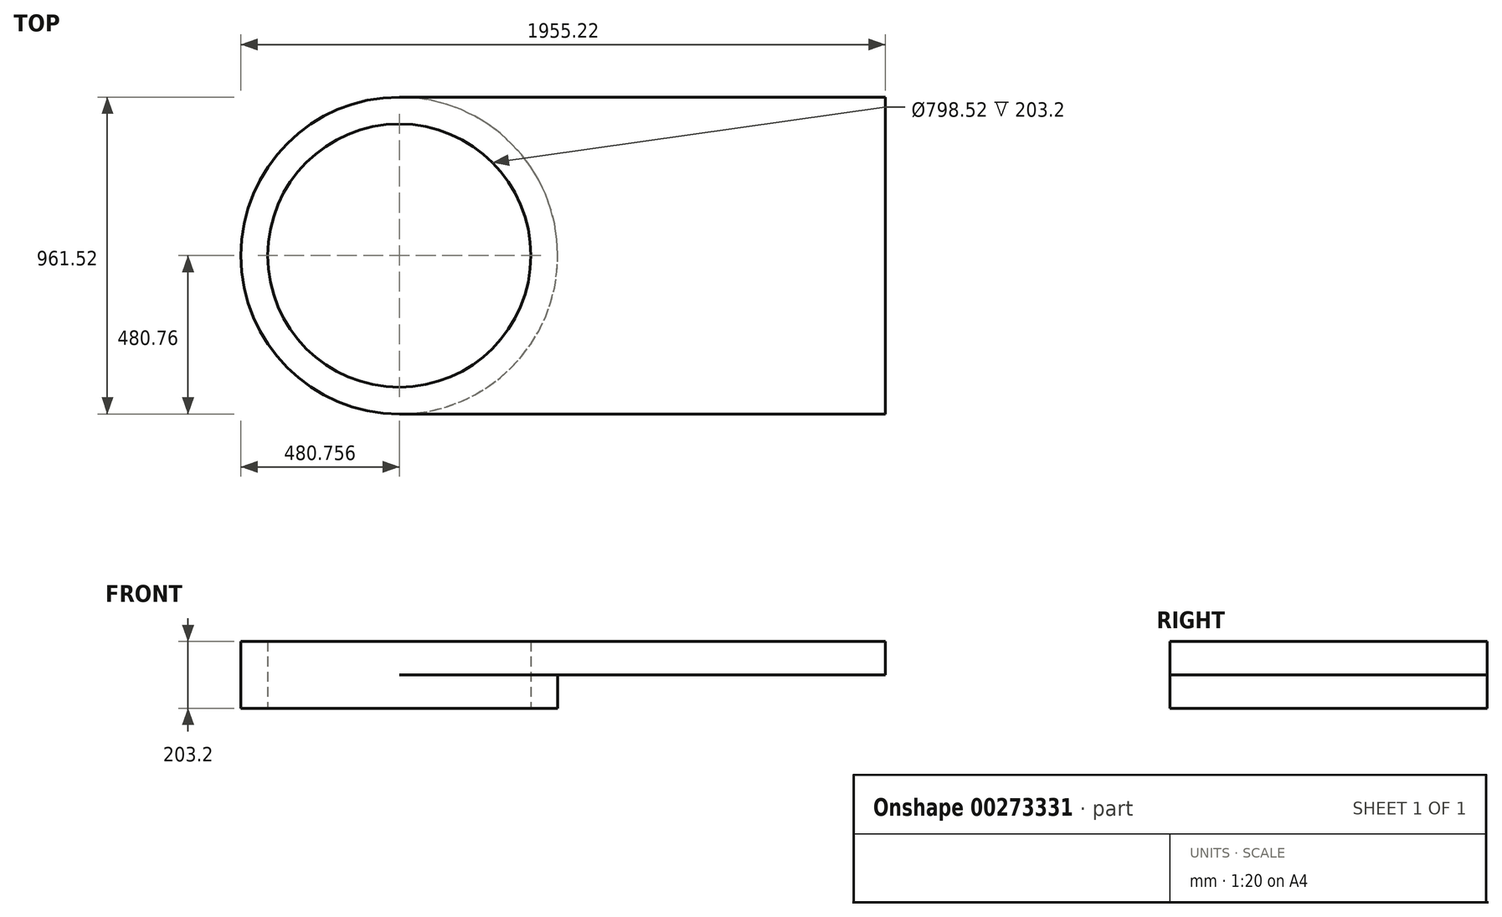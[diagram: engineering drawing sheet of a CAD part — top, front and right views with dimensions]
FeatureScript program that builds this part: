
annotation { "Feature Type Name" : "Feature", "Feature Type Description" : "" }
export const myFeature = defineFeature(function(context is Context, id is Id, definition is map)
    precondition{}
    {
        {
            var Q0;
            Q0=qCreatedBy(makeId("Top.planeOp"),FACE);
            var sketch = newSketch(context, id + "F0", { "sketchPlane" : qUnion([Q0])});
            skLineSegment(sketch, "E0.bottom", {"start": v(737.23, -480.76) * mm, "end": v(-737.23, -480.76) * mm});
            skLineSegment(sketch, "E0.top", {"start": v(737.23, 480.76) * mm, "end": v(-737.23, 480.76) * mm});
            skLineSegment(sketch, "E0.left", {"start": v(737.23, -480.76) * mm, "end": v(737.23, 480.76) * mm});
            skLineSegment(sketch, "E0.right", {"start": v(-737.23, -480.76) * mm, "end": v(-737.23, 480.76) * mm});
            skPoint(sketch, "E0.middle", {"position": v(0, 0) * mm});
            skCircle(sketch, "E1", {"center": v(-737.23, 0) * mm, "radius": 480.76 * mm});
            skCircle(sketch, "E2", {"center": v(-737.23, 0) * mm, "radius": 399.26 * mm});
            skSolve(sketch);
        }
        {
            var Q0;
            {var subQ1=sQuery(id+"F0.wireOp",EDGE,"E0.right");var subQ3=sQuery(id+"F0.wireOp",EDGE,"E2");var subQ4=makeQuery(id+"F0.imprint","INTERSECT",VERTEX,{"disambiguationData":[OD(0.0)],"derivedFrom":[subQ1,subQ3]});Q0=makeQuery(id+"F0.imprint","IMPRINT",FACE,{"disambiguationData":[TD([[makeQuery(id+"F0.imprint","IMPRINT",EDGE,{"disambiguationData":[TD([[subQ4,1.0]])],"derivedFrom":subQ3}),-1.0]])]});}
            var Q1;
            {var subQ1=sQuery(id+"F0.wireOp",EDGE,"E0.right");var subQ3=sQuery(id+"F0.wireOp",EDGE,"E2");var subQ4=makeQuery(id+"F0.imprint","INTERSECT",VERTEX,{"disambiguationData":[OD(0.0)],"derivedFrom":[subQ1,subQ3]});Q1=makeQuery(id+"F0.imprint","IMPRINT",FACE,{"disambiguationData":[TD([[makeQuery(id+"F0.imprint","IMPRINT",EDGE,{"disambiguationData":[TD([[subQ4,-1.0]])],"derivedFrom":subQ3}),-1.0]])]});}
            var Q2;
            {var subQ0=sQuery(id+"F0.wireOp",EDGE,"E0.bottom");Q2=makeQuery(id+"F0.imprint","IMPRINT",FACE,{"disambiguationData":[TD([[makeQuery(id+"F0.imprint","IMPRINT",EDGE,{"derivedFrom":subQ0}),-1.0]])]});}
            extrude(context, id + "F1", {"entities" : qUnion([Q0, Q1, Q2]), "depth" : 101.6 * mm});
        }
        {
            var Q0;
            {var subQ1=sQuery(id+"F0.wireOp",EDGE,"E0.right");var subQ3=sQuery(id+"F0.wireOp",EDGE,"E2");var subQ4=makeQuery(id+"F0.imprint","INTERSECT",VERTEX,{"disambiguationData":[OD(0.0)],"derivedFrom":[subQ1,subQ3]});Q0=makeQuery(id+"F0.imprint","IMPRINT",FACE,{"disambiguationData":[TD([[makeQuery(id+"F0.imprint","IMPRINT",EDGE,{"disambiguationData":[TD([[subQ4,-1.0]])],"derivedFrom":subQ3}),-1.0]])]});}
            var Q1;
            {var subQ1=sQuery(id+"F0.wireOp",EDGE,"E0.right");var subQ3=sQuery(id+"F0.wireOp",EDGE,"E2");var subQ4=makeQuery(id+"F0.imprint","INTERSECT",VERTEX,{"disambiguationData":[OD(0.0)],"derivedFrom":[subQ1,subQ3]});Q1=makeQuery(id+"F0.imprint","IMPRINT",FACE,{"disambiguationData":[TD([[makeQuery(id+"F0.imprint","IMPRINT",EDGE,{"disambiguationData":[TD([[subQ4,1.0]])],"derivedFrom":subQ3}),-1.0]])]});}
            extrude(context, id + "F2", {"entities" : qUnion([Q0, Q1]), "operationType" : NewBodyOperationType.ADD, "oppositeDirection" : true, "depth" : 101.6 * mm});
        }
    });
